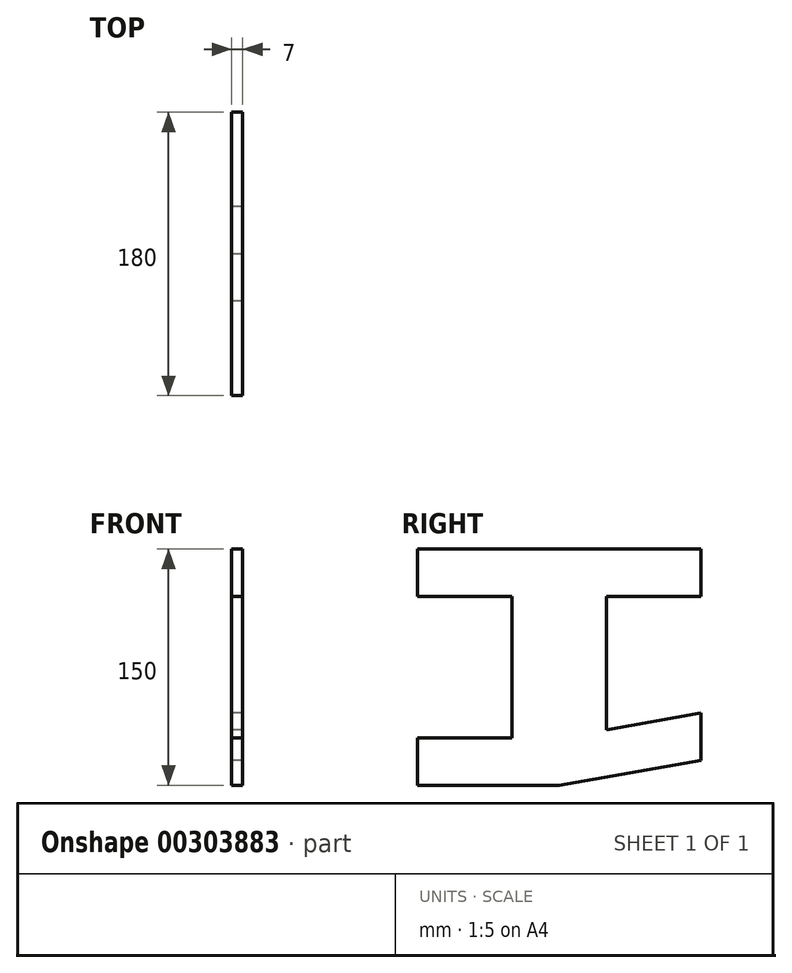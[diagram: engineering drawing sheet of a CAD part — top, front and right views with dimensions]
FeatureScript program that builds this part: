
annotation { "Feature Type Name" : "Feature", "Feature Type Description" : "" }
export const myFeature = defineFeature(function(context is Context, id is Id, definition is map)
    precondition{}
    {
        {
            var Q0;
            Q0=qCreatedBy(makeId("Right.planeOp"),FACE);
            var sketch = newSketch(context, id + "F0", { "sketchPlane" : qUnion([Q0])});
            skLineSegment(sketch, "E0.1", {"start": v(-22.99, 48.81) * mm, "end": v(-82.99, 48.81) * mm});
            skLineSegment(sketch, "E0.3", {"start": v(-22.99, -41.12) * mm, "end": v(-82.99, -41.19) * mm});
            skLineSegment(sketch, "E0.4", {"start": v(-22.99, 48.81) * mm, "end": v(-22.99, -41.12) * mm});
            skLineSegment(sketch, "E1.bottom", {"start": v(-82.99, 48.81) * mm, "end": v(-22.99, 48.81) * mm});
            skLineSegment(sketch, "E1.top", {"start": v(-82.99, 78.81) * mm, "end": v(7.01, 78.81) * mm});
            skLineSegment(sketch, "E1.left", {"start": v(-82.99, 48.81) * mm, "end": v(-82.99, 78.81) * mm});
            skLineSegment(sketch, "E2.left", {"start": v(-22.99, 48.81) * mm, "end": v(-22.99, -41.19) * mm});
            skLineSegment(sketch, "E3.bottom", {"start": v(-82.99, -41.19) * mm, "end": v(-22.99, -41.19) * mm});
            skLineSegment(sketch, "E3.left", {"start": v(-82.99, -41.19) * mm, "end": v(-82.99, -71.19) * mm});
            skLineSegment(sketch, "E4", {"start": v(7.01, 78.81) * mm, "end": v(97.01, 78.81) * mm});
            skLineSegment(sketch, "E5", {"start": v(97.01, 78.81) * mm, "end": v(97.01, 48.81) * mm});
            skLineSegment(sketch, "E6", {"start": v(97.01, 48.81) * mm, "end": v(37.01, 48.81) * mm});
            skLineSegment(sketch, "E7", {"start": v(37.01, 48.81) * mm, "end": v(37.01, -35.9) * mm});
            skLineSegment(sketch, "E8", {"start": v(37.01, -35.9) * mm, "end": v(97.01, -25.32) * mm});
            skLineSegment(sketch, "E9", {"start": v(-82.99, -71.19) * mm, "end": v(7.01, -71.19) * mm});
            skLineSegment(sketch, "E10", {"start": v(7.01, -71.19) * mm, "end": v(97.01, -55.32) * mm});
            skLineSegment(sketch, "E11", {"start": v(97.01, -25.32) * mm, "end": v(97.01, -55.32) * mm});
            skSolve(sketch);
        }
        {
            var Q0;
            Q0=makeQuery(id+"F0.imprint","IMPRINT",FACE,{"disambiguationData":[TD([[makeQuery(id+"F0.imprint","IMPRINT",EDGE,{"derivedFrom":sQuery(id+"F0.wireOp",EDGE,"E1.top")}),-1.0]])]});
            var Q1;
            {var subQ8=sQuery(id+"F0.wireOp",EDGE,"43249994-156e-432a-ab60-bef2d513b2ee.left");Q1=makeQuery(id+"F0.imprint","IMPRINT",FACE,{"disambiguationData":[TD([[makeQuery(id+"F0.imprint","IMPRINT",EDGE,{"derivedFrom":subQ8}),1.0]])]});}
            var Q2;
            {var subQ3=sQuery(id+"F0.wireOp",EDGE,"43249994-156e-432a-ab60-bef2d513b2ee.left");Q2=makeQuery(id+"F0.imprint","IMPRINT",FACE,{"disambiguationData":[TD([[makeQuery(id+"F0.imprint","IMPRINT",EDGE,{"derivedFrom":subQ3}),-1.0]])]});}
            extrude(context, id + "F1", {"entities" : qUnion([Q0, Q1, Q2]), "depth" : 7 * mm});
        }
    });
